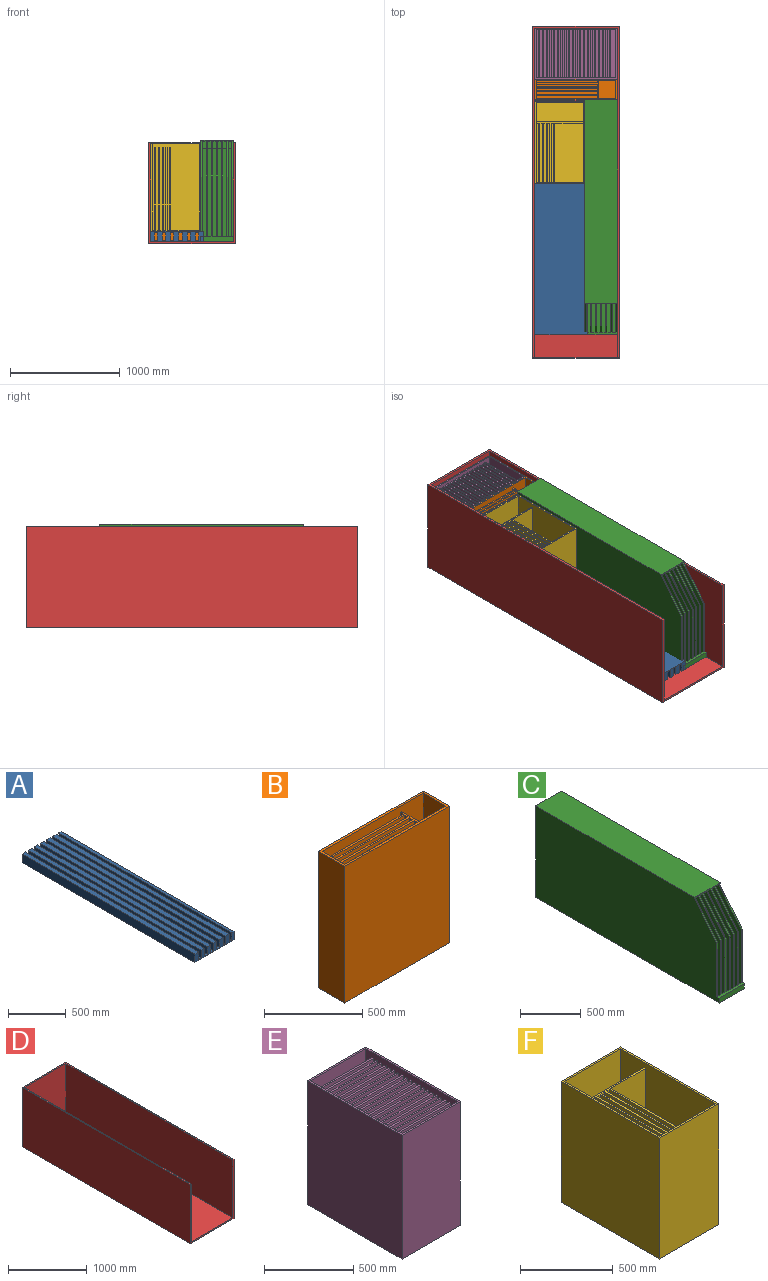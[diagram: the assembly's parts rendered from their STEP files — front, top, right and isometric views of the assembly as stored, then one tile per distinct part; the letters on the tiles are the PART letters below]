
ASSEMBLY  parts=6 mates=5
PART A: 30 faces, bbox 480x2125x92 mm
  f0: plane 2125x45mm, normal (0,0,1), area 95625mm2, adj f6,f7,f8,f27
  f1: plane 2125x45mm, normal (0,0,1), area 95625mm2, adj f6,f8,f25,f28
  f2: plane 2125x45mm, normal (0,0,1), area 95625mm2, adj f6,f8,f22,f24
  f3: plane 2125x45mm, normal (0,0,1), area 95625mm2, adj f6,f8,f19,f21
  f4: plane 2125x45mm, normal (0,0,1), area 95625mm2, adj f6,f8,f16,f18
  f5: plane 2125x45mm, normal (0,0,1), area 95625mm2, adj f6,f8,f13,f15
  f6: plane 480x92mm, normal (0,1,0), area 29760mm2, adj f0,f1,f2,f3,f4,f5,f7,f9
  f7: plane 2125x92mm, normal (-1,0,0), area 195500mm2, adj f0,f6,f8,f11
  f8: plane 480x92mm, normal (0,-1,0), area 29760mm2, adj f0,f1,f2,f3,f4,f5,f7,f9
  f9: plane 2125x92mm, normal (1,0,0), area 195500mm2, adj f6,f8,f10,f11
  f10: plane 2125x30mm, normal (0,0,1), area 63750mm2, adj f6,f8,f9,f12
  f11: plane 2125x480mm, normal (0,0,-1), area 1020000mm2, adj f6,f7,f8,f9
  f12: plane 2125x80mm, normal (-1,0,0), area 170000mm2, adj f6,f8,f10,f14
  f13: plane 2125x80mm, normal (1,0,0), area 170000mm2, adj f5,f6,f8,f14
  f14: plane 2125x30mm, normal (0,0,1), area 63750mm2, adj f6,f8,f12,f13
  f15: plane 2125x80mm, normal (-1,0,0), area 170000mm2, adj f5,f6,f8,f17
  f16: plane 2125x80mm, normal (1,0,0), area 170000mm2, adj f4,f6,f8,f17
  f17: plane 2125x30mm, normal (0,0,1), area 63750mm2, adj f6,f8,f15,f16
  f18: plane 2125x80mm, normal (-1,0,0), area 170000mm2, adj f4,f6,f8,f20
  f19: plane 2125x80mm, normal (1,0,0), area 170000mm2, adj f3,f6,f8,f20
  f20: plane 2125x30mm, normal (0,0,1), area 63750mm2, adj f6,f8,f18,f19
  f21: plane 2125x80mm, normal (-1,0,0), area 170000mm2, adj f3,f6,f8,f23
  f22: plane 2125x80mm, normal (1,0,0), area 170000mm2, adj f2,f6,f8,f23
  f23: plane 2125x30mm, normal (0,0,1), area 63750mm2, adj f6,f8,f21,f22
  f24: plane 2125x80mm, normal (-1,0,0), area 170000mm2, adj f2,f6,f8,f26
  f25: plane 2125x80mm, normal (1,0,0), area 170000mm2, adj f1,f6,f8,f26
  f26: plane 2125x30mm, normal (0,0,1), area 63750mm2, adj f6,f8,f24,f25
  f27: plane 2125x80mm, normal (1,0,0), area 170000mm2, adj f0,f6,f8,f29
  f28: plane 2125x80mm, normal (-1,0,0), area 170000mm2, adj f1,f6,f8,f29
  f29: plane 2125x30mm, normal (0,0,1), area 63750mm2, adj f6,f8,f27,f28
PART B: 31 faces, bbox 750x188x850 mm
  f0: plane 838x726mm, normal (0,-1,0), area 598788mm2, adj f3,f4,f6,f12,f14,f20,f21,f30
  f1: plane 560x22mm, normal (0,0,1), area 12320mm2, adj f12,f26,f27,f28
  f2: plane 560x22mm, normal (0,0,1), area 12320mm2, adj f12,f23,f24,f25
  f3: plane 560x22mm, normal (0,0,1), area 12320mm2, adj f0,f12,f21,f22
  f4: plane 164x154mm, normal (0,0,1), area 25256mm2, adj f0,f13,f14,f20
  f5: plane 560x28mm, normal (0,0,1), area 15680mm2, adj f12,f13,f18,f19
  f6: plane 750x188mm, normal (0,0,1), area 21936mm2, adj f0,f7,f8,f9,f10,f12,f13,f14
  f7: plane 850x750mm, normal (0,1,0), area 637500mm2, adj f6,f8,f10,f11
  f8: plane 850x188mm, normal (-1,0,0), area 159800mm2, adj f6,f7,f9,f11
  f9: plane 850x750mm, normal (0,-1,0), area 637500mm2, adj f6,f8,f10,f11
  f10: plane 850x188mm, normal (1,0,0), area 159800mm2, adj f6,f7,f9,f11
  f11: plane 750x188mm, normal (0,0,-1), area 141000mm2, adj f7,f8,f9,f10
  f12: plane 838x164mm, normal (1,0,0), area 99032mm2, adj f0,f1,f2,f3,f5,f6,f13,f15
  f13: plane 838x726mm, normal (0,1,0), area 598788mm2, adj f4,f5,f6,f12,f14,f19,f20,f30
  f14: plane 838x164mm, normal (-1,0,0), area 137432mm2, adj f0,f4,f6,f13
  f15: plane 560x22mm, normal (0,0,1), area 12320mm2, adj f12,f16,f17,f29
  f16: plane 800x22mm, normal (-1,0,0), area 17600mm2, adj f15,f17,f29,f30
  f17: plane 800x560mm, normal (0,1,0), area 448000mm2, adj f12,f15,f16,f30
  f18: plane 800x560mm, normal (0,-1,0), area 448000mm2, adj f5,f12,f19,f30
  f19: plane 800x28mm, normal (-1,0,0), area 22400mm2, adj f5,f13,f18,f30
  f20: plane 800x164mm, normal (1,0,0), area 131200mm2, adj f0,f4,f13,f30
  f21: plane 800x22mm, normal (-1,0,0), area 17600mm2, adj f0,f3,f22,f30
  f22: plane 800x560mm, normal (0,1,0), area 448000mm2, adj f3,f12,f21,f30
  f23: plane 800x560mm, normal (0,-1,0), area 448000mm2, adj f2,f12,f24,f30
  f24: plane 800x22mm, normal (-1,0,0), area 17600mm2, adj f2,f23,f25,f30
  f25: plane 800x560mm, normal (0,1,0), area 448000mm2, adj f2,f12,f24,f30
  f26: plane 800x560mm, normal (0,-1,0), area 448000mm2, adj f1,f12,f27,f30
  f27: plane 800x22mm, normal (-1,0,0), area 17600mm2, adj f1,f26,f28,f30
  f28: plane 800x560mm, normal (0,1,0), area 448000mm2, adj f1,f12,f27,f30
  f29: plane 800x560mm, normal (0,-1,0), area 448000mm2, adj f12,f15,f16,f30
  f30: plane 572x164mm, normal (0,0,1), area 28848mm2, adj f0,f12,f13,f16,f17,f18,f19,f20
PART C: 85 faces, bbox 298.7x2137x922 mm
  f0: plane 537.35x12mm, normal (0,-1,0), area 6448.2mm2, adj f7,f25,f33,f47
  f1: plane 537.35x12mm, normal (0,-1,0), area 6448.2mm2, adj f23,f26,f33,f46
  f2: plane 537.35x12mm, normal (0,-1,0), area 6448.2mm2, adj f20,f22,f33,f48
  f3: plane 537.35x12mm, normal (0,-1,0), area 6448.2mm2, adj f17,f19,f33,f49
  f4: plane 537.35x12mm, normal (0,-1,0), area 6448.2mm2, adj f14,f16,f33,f50
  f5: plane 537.35x12mm, normal (0,-1,0), area 6448.2mm2, adj f11,f13,f33,f51
  f6: plane 537.35x12mm, normal (0,-1,0), area 6448.2mm2, adj f8,f10,f33,f52
  f7: plane 2137x922mm, normal (-1,0,0), area 1903449.3mm2, adj f0,f9,f33,f34,f42,f44,f47,f59
  f8: plane 2137x910mm, normal (1,0,0), area 1881225.3mm2, adj f6,f9,f33,f34,f45,f52,f59
  f9: plane 2137x294mm, normal (0,0,-1), area 628278mm2, adj f7,f8,f34,f59
  f10: plane 2100x898mm, normal (-1,0,0), area 1843855.3mm2, adj f6,f12,f28,f41,f52,f53
  f11: plane 2100x898mm, normal (1,0,0), area 281808mm2, adj f5,f12,f28,f41,f51,f53,f80,f81
  f12: plane 2100x35mm, normal (0,0,1), area 73500mm2, adj f10,f11,f28,f53
  f13: plane 2100x898mm, normal (-1,0,0), area 281808mm2, adj f5,f15,f29,f40,f51,f54,f80,f81
  f14: plane 2100x898mm, normal (1,0,0), area 281808mm2, adj f4,f15,f29,f40,f50,f54,f75,f76
  f15: plane 2100x35mm, normal (0,0,1), area 73500mm2, adj f13,f14,f29,f54
  f16: plane 2100x898mm, normal (-1,0,0), area 281808mm2, adj f4,f18,f30,f39,f50,f55,f75,f76
  f17: plane 2100x898mm, normal (1,0,0), area 281808mm2, adj f3,f18,f30,f39,f49,f55,f70,f71
  f18: plane 2100x35mm, normal (0,0,1), area 73500mm2, adj f16,f17,f30,f55
  f19: plane 2100x898mm, normal (-1,0,0), area 281808mm2, adj f3,f21,f31,f38,f49,f56,f70,f71
  f20: plane 2100x898mm, normal (1,0,0), area 281808mm2, adj f2,f21,f31,f38,f48,f56,f65,f66
  f21: plane 2100x35mm, normal (0,0,1), area 73500mm2, adj f19,f20,f31,f56
  f22: plane 2100x898mm, normal (-1,0,0), area 281808mm2, adj f2,f24,f35,f37,f48,f57,f65,f66
  f23: plane 2100x898mm, normal (1,0,0), area 281808mm2, adj f1,f24,f35,f37,f46,f57,f60,f61
  f24: plane 2100x35mm, normal (0,0,1), area 73500mm2, adj f22,f23,f35,f57
  f25: plane 2100x898mm, normal (1,0,0), area 1843855.3mm2, adj f0,f27,f32,f36,f47,f58
  f26: plane 2100x898mm, normal (-1,0,0), area 281808mm2, adj f1,f27,f32,f36,f46,f58,f60,f61
  f27: plane 2100x35mm, normal (0,0,1), area 73500mm2, adj f25,f26,f32,f58
  f28: plane 38x35mm, normal (0,1,0), area 1330mm2, adj f10,f11,f12,f33
  f29: plane 38x35mm, normal (0,1,0), area 1330mm2, adj f13,f14,f15,f33
  f30: plane 38x35mm, normal (0,1,0), area 1330mm2, adj f16,f17,f18,f33
  f31: plane 38x35mm, normal (0,1,0), area 1330mm2, adj f19,f20,f21,f33
  f32: plane 38x35mm, normal (0,1,0), area 1330mm2, adj f25,f26,f27,f33
  f33: plane 294x25mm, normal (0,0,1), area 7350mm2, adj f0,f1,f2,f3,f4,f5,f6,f7
  f34: plane 294x50mm, normal (0,-1,0), area 14700mm2, adj f7,f8,f9,f33
  f35: plane 38x35mm, normal (0,1,0), area 1330mm2, adj f22,f23,f24,f33
  f36: plane 1840x35mm, normal (0,0,-1), area 64400mm2, adj f25,f26,f42,f58
  f37: plane 1840x35mm, normal (0,0,-1), area 64400mm2, adj f22,f23,f42,f57
  f38: plane 1840x35mm, normal (0,0,-1), area 64400mm2, adj f19,f20,f42,f56
  f39: plane 1840x35mm, normal (0,0,-1), area 64400mm2, adj f16,f17,f42,f55
  f40: plane 1840x35mm, normal (0,0,-1), area 64400mm2, adj f13,f14,f42,f54
  f41: plane 1840x35mm, normal (0,0,-1), area 64400mm2, adj f10,f11,f42,f53
  f42: plane 298.74x12mm, normal (0,-1,0), area 3584.9mm2, adj f7,f36,f37,f38,f39,f40,f41,f43
  f43: plane 1852x12mm, normal (1,0,0), area 22224mm2, adj f42,f44,f45,f59
  f44: plane 1852x298.74mm, normal (0,0,1), area 553265mm2, adj f7,f42,f43,f59
  f45: plane 1852x4.74mm, normal (0,0,-1), area 8777mm2, adj f8,f42,f43,f59
  f46: plane 322.65x260mm, normal (0,-0.78,0.63), area 4972.5mm2, adj f1,f23,f26,f42
  f47: plane 322.65x260mm, normal (0,-0.78,0.63), area 4972.5mm2, adj f0,f7,f25,f42
  f48: plane 322.65x260mm, normal (0,-0.78,0.63), area 4972.5mm2, adj f2,f20,f22,f42
  f49: plane 322.65x260mm, normal (0,-0.78,0.63), area 4972.5mm2, adj f3,f17,f19,f42
  f50: plane 322.65x260mm, normal (0,-0.78,0.63), area 4972.5mm2, adj f4,f14,f16,f42
  f51: plane 322.65x260mm, normal (0,-0.78,0.63), area 4972.5mm2, adj f5,f11,f13,f42
  f52: plane 322.65x260mm, normal (0,-0.78,0.63), area 4972.5mm2, adj f6,f8,f10,f42
  f53: plane 898x35mm, normal (0,-1,0), area 31430mm2, adj f10,f11,f12,f41
  f54: plane 898x35mm, normal (0,-1,0), area 31430mm2, adj f13,f14,f15,f40
  f55: plane 898x35mm, normal (0,-1,0), area 31430mm2, adj f16,f17,f18,f39
  f56: plane 898x35mm, normal (0,-1,0), area 31430mm2, adj f19,f20,f21,f38
  f57: plane 898x35mm, normal (0,-1,0), area 31430mm2, adj f22,f23,f24,f37
  f58: plane 898x35mm, normal (0,-1,0), area 31430mm2, adj f25,f26,f27,f36
  f59: plane 922x298.74mm, normal (0,1,0), area 271124.9mm2, adj f7,f8,f9,f43,f44,f45
  f60: plane 2000x12mm, normal (0,0,1), area 24000mm2, adj f23,f26,f61,f64
  f61: plane 798x12mm, normal (0,-1,0), area 9576mm2, adj f23,f26,f60,f62
  f62: plane 1766.08x12mm, normal (0,0,-1), area 21192.9mm2, adj f23,f26,f61,f63
  f63: plane 290.29x233.92mm, normal (0,0.78,-0.63), area 4473.7mm2, adj f23,f26,f62,f64
  f64: plane 507.71x12mm, normal (0,1,0), area 6092.5mm2, adj f23,f26,f60,f63
  f65: plane 2000x12mm, normal (0,0,1), area 24000mm2, adj f20,f22,f66,f69
  f66: plane 798x12mm, normal (0,-1,0), area 9576mm2, adj f20,f22,f65,f67
  f67: plane 1766.08x12mm, normal (0,0,-1), area 21192.9mm2, adj f20,f22,f66,f68
  f68: plane 290.29x233.92mm, normal (0,0.78,-0.63), area 4473.7mm2, adj f20,f22,f67,f69
  f69: plane 507.71x12mm, normal (0,1,0), area 6092.5mm2, adj f20,f22,f65,f68
  f70: plane 2000x12mm, normal (0,0,1), area 24000mm2, adj f17,f19,f71,f74
  f71: plane 798x12mm, normal (0,-1,0), area 9576mm2, adj f17,f19,f70,f72
  f72: plane 1766.08x12mm, normal (0,0,-1), area 21192.9mm2, adj f17,f19,f71,f73
  f73: plane 290.29x233.92mm, normal (0,0.78,-0.63), area 4473.7mm2, adj f17,f19,f72,f74
  f74: plane 507.71x12mm, normal (0,1,0), area 6092.5mm2, adj f17,f19,f70,f73
  f75: plane 2000x12mm, normal (0,0,1), area 24000mm2, adj f14,f16,f76,f79
  f76: plane 798x12mm, normal (0,-1,0), area 9576mm2, adj f14,f16,f75,f77
  f77: plane 1766.08x12mm, normal (0,0,-1), area 21192.9mm2, adj f14,f16,f76,f78
  f78: plane 290.29x233.92mm, normal (0,0.78,-0.63), area 4473.7mm2, adj f14,f16,f77,f79
  f79: plane 507.71x12mm, normal (0,1,0), area 6092.5mm2, adj f14,f16,f75,f78
  f80: plane 507.71x12mm, normal (0,1,0), area 6092.5mm2, adj f11,f13,f81,f84
  f81: plane 290.29x233.92mm, normal (0,0.78,-0.63), area 4473.7mm2, adj f11,f13,f80,f82
  f82: plane 1766.08x12mm, normal (0,0,-1), area 21192.9mm2, adj f11,f13,f81,f83
  f83: plane 798x12mm, normal (0,-1,0), area 9576mm2, adj f11,f13,f82,f84
  f84: plane 2000x12mm, normal (0,0,1), area 24000mm2, adj f11,f13,f80,f83
PART D: 10 faces, bbox 790x3020x920 mm
  f0: plane 3020x920mm, normal (1,0,0), area 2778400mm2, adj f1,f2,f7,f9
  f1: plane 3020x790mm, normal (0,0,-1), area 2385800mm2, adj f0,f3,f7,f9
  f2: plane 3020x790mm, normal (0,0,1), area 135800mm2, adj f0,f3,f4,f5,f7,f8,f9
  f3: plane 3020x920mm, normal (-1,0,0), area 2778400mm2, adj f1,f2,f7,f9
  f4: plane 3000x900mm, normal (-1,0,0), area 2700000mm2, adj f2,f6,f8,f9
  f5: plane 3000x900mm, normal (1,0,0), area 2700000mm2, adj f2,f6,f8,f9
  f6: plane 3000x750mm, normal (0,0,1), area 2250000mm2, adj f4,f5,f8,f9
  f7: plane 920x790mm, normal (0,1,0), area 726800mm2, adj f0,f1,f2,f3
  f8: plane 900x750mm, normal (0,-1,0), area 675000mm2, adj f2,f4,f5,f6
  f9: plane 920x790mm, normal (0,-1,0), area 51800mm2, adj f0,f1,f2,f3,f4,f5,f6
PART E: 171 faces, bbox 464x750x850 mm
  f0: plane 440x22mm, normal (0,0,1), area 9680mm2, adj f1,f28,f86,f88
  f1: plane 838x726mm, normal (-1,0,0), area 416388mm2, adj f0,f2,f3,f4,f5,f6,f7,f8
  f2: plane 440x22mm, normal (0,0,1), area 9680mm2, adj f1,f28,f83,f85
  f3: plane 440x22mm, normal (0,0,1), area 9680mm2, adj f1,f28,f80,f82
  f4: plane 440x22mm, normal (0,0,1), area 9680mm2, adj f1,f28,f77,f79
  f5: plane 440x22mm, normal (0,0,1), area 9680mm2, adj f1,f28,f74,f76
  f6: plane 440x22mm, normal (0,0,1), area 9680mm2, adj f1,f28,f71,f73
  f7: plane 440x22mm, normal (0,0,1), area 9680mm2, adj f1,f28,f68,f70
  f8: plane 440x22mm, normal (0,0,1), area 9680mm2, adj f1,f28,f65,f67
  f9: plane 440x22mm, normal (0,0,1), area 9680mm2, adj f1,f28,f62,f64
  f10: plane 440x22mm, normal (0,0,1), area 9680mm2, adj f1,f28,f59,f61
  f11: plane 440x22mm, normal (0,0,1), area 9680mm2, adj f1,f28,f56,f58
  f12: plane 440x22mm, normal (0,0,1), area 9680mm2, adj f1,f28,f53,f55
  f13: plane 440x22mm, normal (0,0,1), area 9680mm2, adj f1,f28,f50,f52
  f14: plane 440x22mm, normal (0,0,1), area 9680mm2, adj f1,f28,f47,f49
  f15: plane 440x22mm, normal (0,0,1), area 9680mm2, adj f1,f28,f44,f46
  f16: plane 440x22mm, normal (0,0,1), area 9680mm2, adj f1,f28,f41,f43
  f17: plane 440x22mm, normal (0,0,1), area 9680mm2, adj f1,f28,f38,f40
  f18: plane 440x22mm, normal (0,0,1), area 9680mm2, adj f1,f28,f35,f37
  f19: plane 440x22mm, normal (0,0,1), area 9680mm2, adj f1,f28,f32,f34
  f20: plane 440x22mm, normal (0,0,1), area 9680mm2, adj f1,f28,f29,f31
  f21: plane 750x464mm, normal (0,0,1), area 28560mm2, adj f1,f22,f23,f24,f25,f27,f28,f29
  f22: plane 850x464mm, normal (0,1,0), area 394400mm2, adj f21,f23,f25,f26
  f23: plane 850x750mm, normal (-1,0,0), area 637500mm2, adj f21,f22,f24,f26
  f24: plane 850x464mm, normal (0,-1,0), area 394400mm2, adj f21,f23,f25,f26
  f25: plane 850x750mm, normal (1,0,0), area 637500mm2, adj f21,f22,f24,f26
  f26: plane 750x464mm, normal (0,0,-1), area 348000mm2, adj f22,f23,f24,f25
  f27: plane 838x440mm, normal (0,-1,0), area 368720mm2, adj f1,f21,f28,f30
  f28: plane 838x726mm, normal (1,0,0), area 416388mm2, adj f0,f2,f3,f4,f5,f6,f7,f8
  f29: plane 838x440mm, normal (0,1,0), area 368720mm2, adj f1,f20,f21,f28
  f30: plane 440x46mm, normal (0,0,1), area 20240mm2, adj f1,f27,f28,f89
  f31: plane 800x440mm, normal (0,-1,0), area 114000mm2, adj f1,f20,f28,f33,f167,f168,f169,f170
  f32: plane 800x440mm, normal (0,1,0), area 114000mm2, adj f1,f19,f28,f33,f167,f168,f169,f170
  f33: plane 440x12mm, normal (0,0,1), area 5280mm2, adj f1,f28,f31,f32
  f34: plane 800x440mm, normal (0,-1,0), area 114000mm2, adj f1,f19,f28,f36,f163,f164,f165,f166
  f35: plane 800x440mm, normal (0,1,0), area 114000mm2, adj f1,f18,f28,f36,f163,f164,f165,f166
  f36: plane 440x12mm, normal (0,0,1), area 5280mm2, adj f1,f28,f34,f35
  f37: plane 800x440mm, normal (0,-1,0), area 114000mm2, adj f1,f18,f28,f39,f159,f160,f161,f162
  f38: plane 800x440mm, normal (0,1,0), area 114000mm2, adj f1,f17,f28,f39,f159,f160,f161,f162
  f39: plane 440x12mm, normal (0,0,1), area 5280mm2, adj f1,f28,f37,f38
  f40: plane 800x440mm, normal (0,-1,0), area 114000mm2, adj f1,f17,f28,f42,f155,f156,f157,f158
  f41: plane 800x440mm, normal (0,1,0), area 114000mm2, adj f1,f16,f28,f42,f155,f156,f157,f158
  f42: plane 440x12mm, normal (0,0,1), area 5280mm2, adj f1,f28,f40,f41
  f43: plane 800x440mm, normal (0,-1,0), area 114000mm2, adj f1,f16,f28,f45,f151,f152,f153,f154
  f44: plane 800x440mm, normal (0,1,0), area 114000mm2, adj f1,f15,f28,f45,f151,f152,f153,f154
  f45: plane 440x12mm, normal (0,0,1), area 5280mm2, adj f1,f28,f43,f44
  f46: plane 800x440mm, normal (0,-1,0), area 114000mm2, adj f1,f15,f28,f48,f147,f148,f149,f150
  f47: plane 800x440mm, normal (0,1,0), area 114000mm2, adj f1,f14,f28,f48,f147,f148,f149,f150
  f48: plane 440x12mm, normal (0,0,1), area 5280mm2, adj f1,f28,f46,f47
  f49: plane 800x440mm, normal (0,-1,0), area 114000mm2, adj f1,f14,f28,f51,f143,f144,f145,f146
  f50: plane 800x440mm, normal (0,1,0), area 114000mm2, adj f1,f13,f28,f51,f143,f144,f145,f146
  f51: plane 440x12mm, normal (0,0,1), area 5280mm2, adj f1,f28,f49,f50
  f52: plane 800x440mm, normal (0,-1,0), area 114000mm2, adj f1,f13,f28,f54,f139,f140,f141,f142
  f53: plane 800x440mm, normal (0,1,0), area 114000mm2, adj f1,f12,f28,f54,f139,f140,f141,f142
  f54: plane 440x12mm, normal (0,0,1), area 5280mm2, adj f1,f28,f52,f53
  f55: plane 800x440mm, normal (0,-1,0), area 114000mm2, adj f1,f12,f28,f57,f135,f136,f137,f138
  f56: plane 800x440mm, normal (0,1,0), area 114000mm2, adj f1,f11,f28,f57,f135,f136,f137,f138
  f57: plane 440x12mm, normal (0,0,1), area 5280mm2, adj f1,f28,f55,f56
  f58: plane 800x440mm, normal (0,-1,0), area 114000mm2, adj f1,f11,f28,f60,f131,f132,f133,f134
  f59: plane 800x440mm, normal (0,1,0), area 114000mm2, adj f1,f10,f28,f60,f131,f132,f133,f134
  f60: plane 440x12mm, normal (0,0,1), area 5280mm2, adj f1,f28,f58,f59
  f61: plane 800x440mm, normal (0,-1,0), area 114000mm2, adj f1,f10,f28,f63,f127,f128,f129,f130
  f62: plane 800x440mm, normal (0,1,0), area 114000mm2, adj f1,f9,f28,f63,f127,f128,f129,f130
  f63: plane 440x12mm, normal (0,0,1), area 5280mm2, adj f1,f28,f61,f62
  f64: plane 800x440mm, normal (0,-1,0), area 114000mm2, adj f1,f9,f28,f66,f123,f124,f125,f126
  f65: plane 800x440mm, normal (0,1,0), area 114000mm2, adj f1,f8,f28,f66,f123,f124,f125,f126
  f66: plane 440x12mm, normal (0,0,1), area 5280mm2, adj f1,f28,f64,f65
  f67: plane 800x440mm, normal (0,-1,0), area 114000mm2, adj f1,f8,f28,f69,f119,f120,f121,f122
  f68: plane 800x440mm, normal (0,1,0), area 114000mm2, adj f1,f7,f28,f69,f119,f120,f121,f122
  f69: plane 440x12mm, normal (0,0,1), area 5280mm2, adj f1,f28,f67,f68
  f70: plane 800x440mm, normal (0,-1,0), area 114000mm2, adj f1,f7,f28,f72,f115,f116,f117,f118
  f71: plane 800x440mm, normal (0,1,0), area 114000mm2, adj f1,f6,f28,f72,f115,f116,f117,f118
  f72: plane 440x12mm, normal (0,0,1), area 5280mm2, adj f1,f28,f70,f71
  f73: plane 800x440mm, normal (0,-1,0), area 114000mm2, adj f1,f6,f28,f75,f111,f112,f113,f114
  f74: plane 800x440mm, normal (0,1,0), area 114000mm2, adj f1,f5,f28,f75,f111,f112,f113,f114
  f75: plane 440x12mm, normal (0,0,1), area 5280mm2, adj f1,f28,f73,f74
  f76: plane 800x440mm, normal (0,-1,0), area 114000mm2, adj f1,f5,f28,f78,f107,f108,f109,f110
  f77: plane 800x440mm, normal (0,1,0), area 114000mm2, adj f1,f4,f28,f78,f107,f108,f109,f110
  f78: plane 440x12mm, normal (0,0,1), area 5280mm2, adj f1,f28,f76,f77
  f79: plane 800x440mm, normal (0,-1,0), area 114000mm2, adj f1,f4,f28,f81,f103,f104,f105,f106
  f80: plane 800x440mm, normal (0,1,0), area 114000mm2, adj f1,f3,f28,f81,f103,f104,f105,f106
  f81: plane 440x12mm, normal (0,0,1), area 5280mm2, adj f1,f28,f79,f80
  f82: plane 800x440mm, normal (0,-1,0), area 114000mm2, adj f1,f3,f28,f84,f99,f100,f101,f102
  f83: plane 800x440mm, normal (0,1,0), area 114000mm2, adj f1,f2,f28,f84,f99,f100,f101,f102
  f84: plane 440x12mm, normal (0,0,1), area 5280mm2, adj f1,f28,f82,f83
  f85: plane 800x440mm, normal (0,-1,0), area 114000mm2, adj f1,f2,f28,f87,f95,f96,f97,f98
  f86: plane 800x440mm, normal (0,1,0), area 114000mm2, adj f0,f1,f28,f87,f95,f96,f97,f98
  f87: plane 440x12mm, normal (0,0,1), area 5280mm2, adj f1,f28,f85,f86
  f88: plane 800x440mm, normal (0,-1,0), area 114000mm2, adj f0,f1,f28,f90,f91,f92,f93,f94
  f89: plane 800x440mm, normal (0,1,0), area 114000mm2, adj f1,f28,f30,f90,f91,f92,f93,f94
  f90: plane 440x12mm, normal (0,0,1), area 5280mm2, adj f1,f28,f88,f89
  f91: plane 340x12mm, normal (0,0,-1), area 4080mm2, adj f88,f89,f92,f94
  f92: plane 700x12mm, normal (1,0,0), area 8400mm2, adj f88,f89,f91,f93
  f93: plane 340x12mm, normal (0,0,1), area 4080mm2, adj f88,f89,f92,f94
  f94: plane 700x12mm, normal (-1,0,0), area 8400mm2, adj f88,f89,f91,f93
  f95: plane 340x12mm, normal (0,0,-1), area 4080mm2, adj f85,f86,f96,f98
  f96: plane 700x12mm, normal (1,0,0), area 8400mm2, adj f85,f86,f95,f97
  f97: plane 340x12mm, normal (0,0,1), area 4080mm2, adj f85,f86,f96,f98
  f98: plane 700x12mm, normal (-1,0,0), area 8400mm2, adj f85,f86,f95,f97
  f99: plane 340x12mm, normal (0,0,-1), area 4080mm2, adj f82,f83,f100,f102
  f100: plane 700x12mm, normal (1,0,0), area 8400mm2, adj f82,f83,f99,f101
  f101: plane 340x12mm, normal (0,0,1), area 4080mm2, adj f82,f83,f100,f102
  f102: plane 700x12mm, normal (-1,0,0), area 8400mm2, adj f82,f83,f99,f101
  f103: plane 340x12mm, normal (0,0,-1), area 4080mm2, adj f79,f80,f104,f106
  f104: plane 700x12mm, normal (1,0,0), area 8400mm2, adj f79,f80,f103,f105
  f105: plane 340x12mm, normal (0,0,1), area 4080mm2, adj f79,f80,f104,f106
  f106: plane 700x12mm, normal (-1,0,0), area 8400mm2, adj f79,f80,f103,f105
  f107: plane 340x12mm, normal (0,0,-1), area 4080mm2, adj f76,f77,f108,f110
  f108: plane 700x12mm, normal (1,0,0), area 8400mm2, adj f76,f77,f107,f109
  f109: plane 340x12mm, normal (0,0,1), area 4080mm2, adj f76,f77,f108,f110
  f110: plane 700x12mm, normal (-1,0,0), area 8400mm2, adj f76,f77,f107,f109
  f111: plane 340x12mm, normal (0,0,-1), area 4080mm2, adj f73,f74,f112,f114
  f112: plane 700x12mm, normal (1,0,0), area 8400mm2, adj f73,f74,f111,f113
  f113: plane 340x12mm, normal (0,0,1), area 4080mm2, adj f73,f74,f112,f114
  f114: plane 700x12mm, normal (-1,0,0), area 8400mm2, adj f73,f74,f111,f113
  f115: plane 340x12mm, normal (0,0,-1), area 4080mm2, adj f70,f71,f116,f118
  f116: plane 700x12mm, normal (1,0,0), area 8400mm2, adj f70,f71,f115,f117
  f117: plane 340x12mm, normal (0,0,1), area 4080mm2, adj f70,f71,f116,f118
  f118: plane 700x12mm, normal (-1,0,0), area 8400mm2, adj f70,f71,f115,f117
  f119: plane 340x12mm, normal (0,0,-1), area 4080mm2, adj f67,f68,f120,f122
  f120: plane 700x12mm, normal (1,0,0), area 8400mm2, adj f67,f68,f119,f121
  f121: plane 340x12mm, normal (0,0,1), area 4080mm2, adj f67,f68,f120,f122
  f122: plane 700x12mm, normal (-1,0,0), area 8400mm2, adj f67,f68,f119,f121
  f123: plane 340x12mm, normal (0,0,-1), area 4080mm2, adj f64,f65,f124,f126
  f124: plane 700x12mm, normal (1,0,0), area 8400mm2, adj f64,f65,f123,f125
  f125: plane 340x12mm, normal (0,0,1), area 4080mm2, adj f64,f65,f124,f126
  f126: plane 700x12mm, normal (-1,0,0), area 8400mm2, adj f64,f65,f123,f125
  f127: plane 340x12mm, normal (0,0,-1), area 4080mm2, adj f61,f62,f128,f130
  f128: plane 700x12mm, normal (1,0,0), area 8400mm2, adj f61,f62,f127,f129
  f129: plane 340x12mm, normal (0,0,1), area 4080mm2, adj f61,f62,f128,f130
  f130: plane 700x12mm, normal (-1,0,0), area 8400mm2, adj f61,f62,f127,f129
  f131: plane 340x12mm, normal (0,0,-1), area 4080mm2, adj f58,f59,f132,f134
  f132: plane 700x12mm, normal (1,0,0), area 8400mm2, adj f58,f59,f131,f133
  f133: plane 340x12mm, normal (0,0,1), area 4080mm2, adj f58,f59,f132,f134
  f134: plane 700x12mm, normal (-1,0,0), area 8400mm2, adj f58,f59,f131,f133
  f135: plane 340x12mm, normal (0,0,-1), area 4080mm2, adj f55,f56,f136,f138
  f136: plane 700x12mm, normal (1,0,0), area 8400mm2, adj f55,f56,f135,f137
  f137: plane 340x12mm, normal (0,0,1), area 4080mm2, adj f55,f56,f136,f138
  f138: plane 700x12mm, normal (-1,0,0), area 8400mm2, adj f55,f56,f135,f137
  f139: plane 340x12mm, normal (0,0,-1), area 4080mm2, adj f52,f53,f140,f142
  f140: plane 700x12mm, normal (1,0,0), area 8400mm2, adj f52,f53,f139,f141
  f141: plane 340x12mm, normal (0,0,1), area 4080mm2, adj f52,f53,f140,f142
  f142: plane 700x12mm, normal (-1,0,0), area 8400mm2, adj f52,f53,f139,f141
  f143: plane 340x12mm, normal (0,0,-1), area 4080mm2, adj f49,f50,f144,f146
  f144: plane 700x12mm, normal (1,0,0), area 8400mm2, adj f49,f50,f143,f145
  f145: plane 340x12mm, normal (0,0,1), area 4080mm2, adj f49,f50,f144,f146
  f146: plane 700x12mm, normal (-1,0,0), area 8400mm2, adj f49,f50,f143,f145
  f147: plane 340x12mm, normal (0,0,-1), area 4080mm2, adj f46,f47,f148,f150
  f148: plane 700x12mm, normal (1,0,0), area 8400mm2, adj f46,f47,f147,f149
  f149: plane 340x12mm, normal (0,0,1), area 4080mm2, adj f46,f47,f148,f150
  f150: plane 700x12mm, normal (-1,0,0), area 8400mm2, adj f46,f47,f147,f149
  f151: plane 340x12mm, normal (0,0,-1), area 4080mm2, adj f43,f44,f152,f154
  f152: plane 700x12mm, normal (1,0,0), area 8400mm2, adj f43,f44,f151,f153
  f153: plane 340x12mm, normal (0,0,1), area 4080mm2, adj f43,f44,f152,f154
  f154: plane 700x12mm, normal (-1,0,0), area 8400mm2, adj f43,f44,f151,f153
  f155: plane 340x12mm, normal (0,0,-1), area 4080mm2, adj f40,f41,f156,f158
  f156: plane 700x12mm, normal (1,0,0), area 8400mm2, adj f40,f41,f155,f157
  f157: plane 340x12mm, normal (0,0,1), area 4080mm2, adj f40,f41,f156,f158
  f158: plane 700x12mm, normal (-1,0,0), area 8400mm2, adj f40,f41,f155,f157
  f159: plane 340x12mm, normal (0,0,-1), area 4080mm2, adj f37,f38,f160,f162
  f160: plane 700x12mm, normal (1,0,0), area 8400mm2, adj f37,f38,f159,f161
  f161: plane 340x12mm, normal (0,0,1), area 4080mm2, adj f37,f38,f160,f162
  f162: plane 700x12mm, normal (-1,0,0), area 8400mm2, adj f37,f38,f159,f161
  f163: plane 340x12mm, normal (0,0,-1), area 4080mm2, adj f34,f35,f164,f166
  f164: plane 700x12mm, normal (1,0,0), area 8400mm2, adj f34,f35,f163,f165
  f165: plane 340x12mm, normal (0,0,1), area 4080mm2, adj f34,f35,f164,f166
  f166: plane 700x12mm, normal (-1,0,0), area 8400mm2, adj f34,f35,f163,f165
  f167: plane 700x12mm, normal (-1,0,0), area 8400mm2, adj f31,f32,f168,f170
  f168: plane 340x12mm, normal (0,0,1), area 4080mm2, adj f31,f32,f167,f169
  f169: plane 700x12mm, normal (1,0,0), area 8400mm2, adj f31,f32,f168,f170
  f170: plane 340x12mm, normal (0,0,-1), area 4080mm2, adj f31,f32,f167,f169
PART F: 55 faces, bbox 456x750x800 mm
  f0: plane 788x726mm, normal (-1,0,0), area 563088mm2, adj f2,f6,f7,f13,f15,f30,f31,f34
  f1: plane 540x22mm, normal (0,0,1), area 11880mm2, adj f14,f15,f32,f33
  f2: plane 432x174mm, normal (0,0,1), area 75168mm2, adj f0,f13,f14,f31
  f3: plane 540x22mm, normal (0,0,1), area 11880mm2, adj f15,f26,f27,f28
  f4: plane 540x22mm, normal (0,0,1), area 11880mm2, adj f15,f23,f24,f25
  f5: plane 540x22mm, normal (0,0,1), area 11880mm2, adj f15,f20,f21,f22
  f6: plane 540x262mm, normal (0,0,1), area 141480mm2, adj f0,f15,f29,f30
  f7: plane 750x456mm, normal (0,0,1), area 28368mm2, adj f0,f8,f9,f10,f11,f13,f14,f15
  f8: plane 800x456mm, normal (0,1,0), area 364800mm2, adj f7,f9,f11,f12
  f9: plane 800x750mm, normal (-1,0,0), area 600000mm2, adj f7,f8,f10,f12
  f10: plane 800x456mm, normal (0,-1,0), area 364800mm2, adj f7,f9,f11,f12
  f11: plane 800x750mm, normal (1,0,0), area 600000mm2, adj f7,f8,f10,f12
  f12: plane 750x456mm, normal (0,0,-1), area 342000mm2, adj f8,f9,f10,f11
  f13: plane 788x432mm, normal (0,-1,0), area 340416mm2, adj f0,f2,f7,f14
  f14: plane 788x726mm, normal (1,0,0), area 563088mm2, adj f1,f2,f7,f13,f15,f31,f32,f34
  f15: plane 788x432mm, normal (0,1,0), area 295416mm2, adj f0,f1,f3,f4,f5,f6,f7,f14
  f16: plane 540x22mm, normal (0,0,1), area 11880mm2, adj f15,f17,f18,f19
  f17: plane 750x540mm, normal (1,0,0), area 119000mm2, adj f15,f16,f18,f34,f35,f36,f37,f38
  f18: plane 750x22mm, normal (0,-1,0), area 16500mm2, adj f16,f17,f19,f34
  f19: plane 750x540mm, normal (-1,0,0), area 119000mm2, adj f15,f16,f18,f34,f51,f52,f53,f54
  f20: plane 750x540mm, normal (1,0,0), area 119000mm2, adj f5,f15,f21,f34,f51,f52,f53,f54
  f21: plane 750x22mm, normal (0,-1,0), area 16500mm2, adj f5,f20,f22,f34
  f22: plane 750x540mm, normal (-1,0,0), area 119000mm2, adj f5,f15,f21,f34,f47,f48,f49,f50
  f23: plane 750x540mm, normal (1,0,0), area 119000mm2, adj f4,f15,f24,f34,f47,f48,f49,f50
  f24: plane 750x22mm, normal (0,-1,0), area 16500mm2, adj f4,f23,f25,f34
  f25: plane 750x540mm, normal (-1,0,0), area 119000mm2, adj f4,f15,f24,f34,f43,f44,f45,f46
  f26: plane 750x540mm, normal (1,0,0), area 119000mm2, adj f3,f15,f27,f34,f43,f44,f45,f46
  f27: plane 750x22mm, normal (0,-1,0), area 16500mm2, adj f3,f26,f28,f34
  f28: plane 750x540mm, normal (-1,0,0), area 119000mm2, adj f3,f15,f27,f34,f39,f40,f41,f42
  f29: plane 750x540mm, normal (1,0,0), area 119000mm2, adj f6,f15,f30,f34,f39,f40,f41,f42
  f30: plane 750x262mm, normal (0,-1,0), area 196500mm2, adj f0,f6,f29,f34
  f31: plane 750x432mm, normal (0,1,0), area 324000mm2, adj f0,f2,f14,f34
  f32: plane 750x22mm, normal (0,-1,0), area 16500mm2, adj f1,f14,f33,f34
  f33: plane 750x540mm, normal (-1,0,0), area 119000mm2, adj f1,f15,f32,f34,f35,f36,f37,f38
  f34: plane 552x432mm, normal (0,0,1), area 37584mm2, adj f0,f14,f15,f17,f18,f19,f20,f21
  f35: plane 440x12mm, normal (0,0,-1), area 5280mm2, adj f17,f33,f36,f38
  f36: plane 650x12mm, normal (0,-1,0), area 7800mm2, adj f17,f33,f35,f37
  f37: plane 440x12mm, normal (0,0,1), area 5280mm2, adj f17,f33,f36,f38
  f38: plane 650x12mm, normal (0,1,0), area 7800mm2, adj f17,f33,f35,f37
  f39: plane 440x12mm, normal (0,0,-1), area 5280mm2, adj f28,f29,f40,f42
  f40: plane 650x12mm, normal (0,-1,0), area 7800mm2, adj f28,f29,f39,f41
  f41: plane 440x12mm, normal (0,0,1), area 5280mm2, adj f28,f29,f40,f42
  f42: plane 650x12mm, normal (0,1,0), area 7800mm2, adj f28,f29,f39,f41
  f43: plane 440x12mm, normal (0,0,-1), area 5280mm2, adj f25,f26,f44,f46
  f44: plane 650x12mm, normal (0,-1,0), area 7800mm2, adj f25,f26,f43,f45
  f45: plane 440x12mm, normal (0,0,1), area 5280mm2, adj f25,f26,f44,f46
  f46: plane 650x12mm, normal (0,1,0), area 7800mm2, adj f25,f26,f43,f45
  f47: plane 440x12mm, normal (0,0,-1), area 5280mm2, adj f22,f23,f48,f50
  f48: plane 650x12mm, normal (0,-1,0), area 7800mm2, adj f22,f23,f47,f49
  f49: plane 440x12mm, normal (0,0,1), area 5280mm2, adj f22,f23,f48,f50
  f50: plane 650x12mm, normal (0,1,0), area 7800mm2, adj f22,f23,f47,f49
  f51: plane 650x12mm, normal (0,1,0), area 7800mm2, adj f19,f20,f52,f54
  f52: plane 440x12mm, normal (0,0,1), area 5280mm2, adj f19,f20,f51,f53
  f53: plane 650x12mm, normal (0,-1,0), area 7800mm2, adj f19,f20,f52,f54
  f54: plane 440x12mm, normal (0,0,-1), area 5280mm2, adj f19,f20,f51,f53
PLACE A rot(axis=(0,1,0),180deg) t=(-474.88,-131.77,92.44)mm
PLACE B t=(-339.88,1037.73,0.44)mm
PLACE C t=(-111.88,-118.27,0.44)mm
PLACE D t=(-339.88,90.73,-19.56)mm fixed
PLACE E rot(axis=(0,0,-1),90deg) t=(-339.88,1363.73,0.44)mm
PLACE F t=(-486.88,555.73,92.44)mm
MATE fastened F.f12 <-> A.f11  axis (0,0,-1) through (-714.88,930.73,92.44)mm
MATE fastened E.f23 <-> D.f8  axis (0,1,0) through (-714.88,1595.73,0.44)mm
MATE fastened A.f10 <-> D.f6  axis (0,0,-1) through (-714.88,-1194.27,0.44)mm
MATE fastened C.f59 <-> B.f9  axis (0,1,0) through (35.12,943.73,0.44)mm
MATE fastened B.f7 <-> E.f25  axis (0,1,0) through (-714.88,1131.73,0.44)mm
